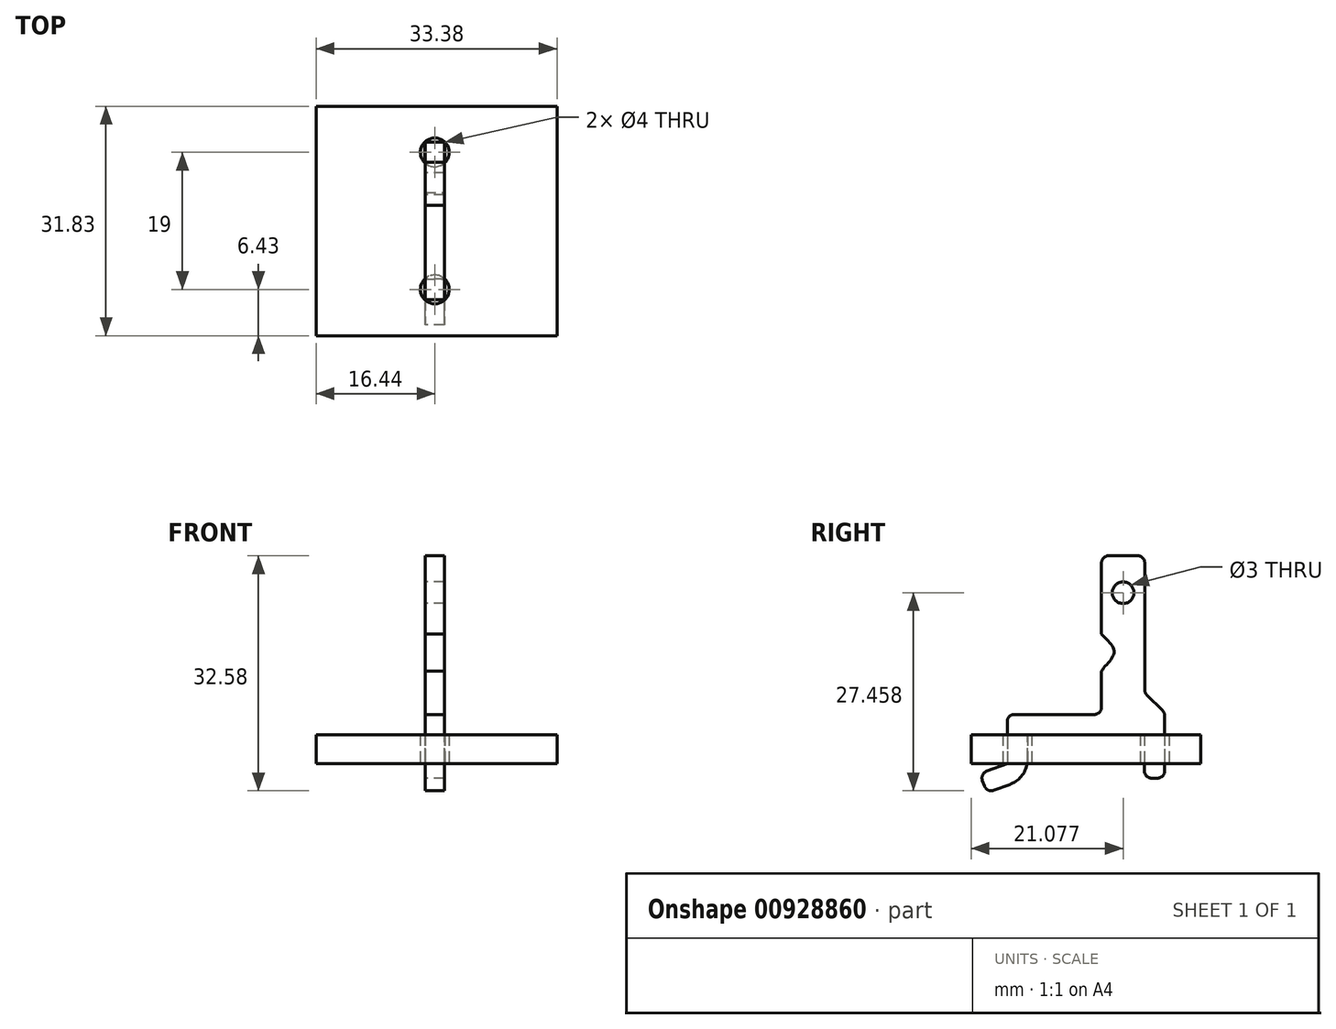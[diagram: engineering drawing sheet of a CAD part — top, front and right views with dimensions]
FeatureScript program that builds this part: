
annotation { "Feature Type Name" : "Feature", "Feature Type Description" : "" }
export const myFeature = defineFeature(function(context is Context, id is Id, definition is map)
    precondition{}
    {
        {
            assignVariable(context, id + "F0", {"name" : "BoardThickness", "anyValue" : 4});
        }
        {
            var Q0;
            Q0=qCreatedBy(makeId("Top.planeOp"),FACE);
            var sketch = newSketch(context, id + "F1", { "sketchPlane" : qUnion([Q0])});
            skCircle(sketch, "E0.cCircle", {"center": v(0, 0) * mm, "radius": 2 * mm});
            skLineSegment(sketch, "E0.0", {"start": v(1.41, 1.41) * mm, "end": v(1.41, -1.41) * mm});
            skLineSegment(sketch, "E0.1", {"start": v(1.41, -1.41) * mm, "end": v(-1.41, -1.41) * mm});
            skLineSegment(sketch, "E0.2", {"start": v(-1.41, -1.41) * mm, "end": v(-1.41, 1.41) * mm});
            skLineSegment(sketch, "E0.3", {"start": v(-1.41, 1.41) * mm, "end": v(1.41, 1.41) * mm});
            skCircle(sketch, "E1.cCircle", {"center": v(0, 19) * mm, "radius": 2 * mm});
            skLineSegment(sketch, "E1.0", {"start": v(1.41, 20.41) * mm, "end": v(1.41, 17.59) * mm});
            skLineSegment(sketch, "E1.1", {"start": v(1.41, 17.59) * mm, "end": v(-1.41, 17.59) * mm});
            skLineSegment(sketch, "E1.2", {"start": v(-1.41, 17.59) * mm, "end": v(-1.41, 20.41) * mm});
            skLineSegment(sketch, "E1.3", {"start": v(-1.41, 20.41) * mm, "end": v(1.41, 20.41) * mm});
            skLineSegment(sketch, "E2.bottom", {"start": v(-16.44, 25.4) * mm, "end": v(16.94, 25.4) * mm});
            skLineSegment(sketch, "E2.top", {"start": v(-16.44, -6.43) * mm, "end": v(16.94, -6.43) * mm});
            skLineSegment(sketch, "E2.left", {"start": v(-16.44, 25.4) * mm, "end": v(-16.44, -6.43) * mm});
            skLineSegment(sketch, "E2.right", {"start": v(16.94, 25.4) * mm, "end": v(16.94, -6.43) * mm});
            skSolve(sketch);
        }
        {
            var Q0;
            Q0=makeQuery(id+"F1.imprint","IMPRINT",FACE,{"disambiguationData":[TD([[makeQuery(id+"F1.imprint","IMPRINT",EDGE,{"derivedFrom":sQuery(id+"F1.wireOp",EDGE,"E2.bottom")}),-1.0]])]});
            extrude(context, id + "F2", {"entities" : qUnion([Q0]), "flatOperationType" : FlatOperationType.REMOVE, "depth" : (getVariable(context, 'BoardThickness')) * mm, "offsetDistance" : 25 * mm, "domain" : OperationDomain.MODEL});
        }
        {
            var Q0;
            Q0=makeQuery(id+"F1.imprint","IMPRINT",FACE,{"disambiguationData":[TD([[makeQuery(id+"F1.imprint","IMPRINT",EDGE,{"derivedFrom":sQuery(id+"F1.wireOp",EDGE,"E0.0")}),-1.0]])]});
            var Q1;
            Q1=makeQuery(id+"F1.imprint","IMPRINT",FACE,{"disambiguationData":[TD([[makeQuery(id+"F1.imprint","IMPRINT",EDGE,{"derivedFrom":sQuery(id+"F1.wireOp",EDGE,"E1.0")}),-1.0]])]});
            extrude(context, id + "F3", {"entities" : qUnion([Q0, Q1]), "flatOperationType" : FlatOperationType.REMOVE, "depth" : 4 * mm, "offsetDistance" : 25 * mm, "domain" : OperationDomain.MODEL});
        }
        {
            var Q0;
            Q0=qCreatedBy(makeId("Right.planeOp"),FACE);
            var sketch = newSketch(context, id + "F4", { "sketchPlane" : qUnion([Q0])});
            skLineSegment(sketch, "E3.0", {"start": v(-1.41, 4) * mm, "end": v(-1.41, 0) * mm});
            skLineSegment(sketch, "E4.0", {"start": v(17.59, 4) * mm, "end": v(17.59, 0) * mm});
            skLineSegment(sketch, "E5.0", {"start": v(1.41, 4) * mm, "end": v(1.41, 0) * mm});
            skLineSegment(sketch, "E6.0", {"start": v(20.41, 4) * mm, "end": v(20.41, 0) * mm});
            skLineSegment(sketch, "E7", {"start": v(1.41, 4) * mm, "end": v(17.59, 4) * mm});
            skLineSegment(sketch, "E8", {"start": v(-1.41, 6.83) * mm, "end": v(11.65, 6.83) * mm});
            skLineSegment(sketch, "E9", {"start": v(11.65, 6.83) * mm, "end": v(11.65, 12.83) * mm});
            skFitSpline(sketch, "E10", {"points": [v(11.65, 12.83) * mm, v(13.41, 15.55) * mm, v(11.65, 17.98) * mm], "startDerivative": vector(3.1, 5.14) * mm, "endDerivative": vector(-3.23, 3.95) * mm});
            skLineSegment(sketch, "E11", {"start": v(11.65, 17.98) * mm, "end": v(11.65, 28.83) * mm});
            skLineSegment(sketch, "E12", {"start": v(11.65, 28.83) * mm, "end": v(17.65, 28.83) * mm});
            skLineSegment(sketch, "E13", {"start": v(17.65, 28.83) * mm, "end": v(17.65, 6.83) * mm});
            skLineSegment(sketch, "E14", {"start": v(17.65, 6.83) * mm, "end": v(20.41, 6.83) * mm});
            skLineSegment(sketch, "E15", {"start": v(20.41, 6.83) * mm, "end": v(20.41, 4) * mm});
            skLineSegment(sketch, "E16", {"start": v(20.41, 0) * mm, "end": v(20.41, -2) * mm});
            skLineSegment(sketch, "E17", {"start": v(20.41, -2) * mm, "end": v(17.59, -2) * mm});
            skLineSegment(sketch, "E18", {"start": v(17.59, -2) * mm, "end": v(17.59, 0) * mm});
            skLineSegment(sketch, "E19", {"start": v(-1.41, 6.83) * mm, "end": v(-1.41, 4) * mm});
            skLineSegment(sketch, "E20", {"start": v(-1.41, 0) * mm, "end": v(-5.2, -1.38) * mm});
            skLineSegment(sketch, "E21", {"start": v(-5.2, -1.38) * mm, "end": v(-4.23, -4.03) * mm});
            skLineSegment(sketch, "E22", {"start": v(-4.23, -4.03) * mm, "end": v(1.41, -1.98) * mm});
            skLineSegment(sketch, "E23", {"start": v(1.41, -1.98) * mm, "end": v(1.41, 0) * mm});
            skCircle(sketch, "E24", {"center": v(14.65, 23.7) * mm, "radius": 1.5 * mm});
            skPoint(sketch, "E24.centerSnap0", {"position": v(14.65, 28.83) * mm});
            skSolve(sketch);
        }
        {
            var Q0;
            Q0=makeQuery(id+"F4.imprint","IMPRINT",FACE,{"disambiguationData":[TD([[makeQuery(id+"F4.imprint","IMPRINT",EDGE,{"derivedFrom":sQuery(id+"F4.wireOp",EDGE,"E3.0")}),1.0]])]});
            extrude(context, id + "F5", {"entities" : qUnion([Q0]), "depth" : 2.7 * mm, "offsetDistance" : 25 * mm, "symmetric" : true});
        }
        {
            var Q0;
            Q0=makeQuery(id+"F5.opExtrude","SWEPT_EDGE",EDGE,{"disambiguationData":[OSD([sQuery(id+"F4.wireOp",EDGE,"E13"),sQuery(id+"F4.wireOp",EDGE,"E14")])]});
            chamfer(context, id + "F6", {"entities" : qUnion([Q0]), "width" : 3 * mm, "tangentPropagation" : true});
        }
        {
            var Q0;
            Q0=makeQuery(id+"F5.opExtrude","SWEPT_EDGE",EDGE,{"disambiguationData":[OSD([sQuery(id+"F4.wireOp",EDGE,"E22"),sQuery(id+"F4.wireOp",EDGE,"E23")])]});
            fillet(context, id + "F7", {"entities" : qUnion([Q0]), "radius" : 3.8 * mm, "tangentPropagation" : true, "allowEdgeOverflow" : false});
        }
        {
            var Q0;
            Q0=makeQuery(id+"F5.opExtrude","SWEPT_EDGE",EDGE,{"disambiguationData":[OSD([sQuery(id+"F4.wireOp",EDGE,"E20"),sQuery(id+"F4.wireOp",EDGE,"E21")])]});
            var Q1;
            Q1=makeQuery(id+"F5.opExtrude","SWEPT_EDGE",EDGE,{"disambiguationData":[OSD([sQuery(id+"F4.wireOp",EDGE,"E21"),sQuery(id+"F4.wireOp",EDGE,"E22")])]});
            var Q2;
            Q2=makeQuery(id+"F5.opExtrude","SWEPT_EDGE",EDGE,{"disambiguationData":[OSD([sQuery(id+"F4.wireOp",EDGE,"E8"),sQuery(id+"F4.wireOp",EDGE,"E19")])]});
            var Q3;
            Q3=makeQuery(id+"F5.opExtrude","SWEPT_EDGE",EDGE,{"disambiguationData":[OSD([sQuery(id+"F4.wireOp",EDGE,"E8"),sQuery(id+"F4.wireOp",EDGE,"E9")])]});
            var Q4;
            Q4=makeQuery(id+"F5.opExtrude","SWEPT_EDGE",EDGE,{"disambiguationData":[OSD([sQuery(id+"F4.wireOp",EDGE,"E11"),sQuery(id+"F4.wireOp",EDGE,"E12")])]});
            var Q5;
            Q5=makeQuery(id+"F5.opExtrude","SWEPT_EDGE",EDGE,{"disambiguationData":[OSD([sQuery(id+"F4.wireOp",EDGE,"E12"),sQuery(id+"F4.wireOp",EDGE,"E13")])]});
            var Q6;
            Q6=makeQuery(id+"F5.opExtrude","SWEPT_EDGE",EDGE,{"disambiguationData":[OSD([sQuery(id+"F4.wireOp",EDGE,"E17"),sQuery(id+"F4.wireOp",EDGE,"E18")])]});
            var Q7;
            Q7=makeQuery(id+"F5.opExtrude","SWEPT_EDGE",EDGE,{"disambiguationData":[OSD([sQuery(id+"F4.wireOp",EDGE,"E16"),sQuery(id+"F4.wireOp",EDGE,"E17")])]});
            var Q8;
            Q8=makeQuery(id+"F6.opChamfer","BLEND_EDGE",EDGE,{"blendedFrom":[makeQuery(id+"F5.opExtrude","SWEPT_EDGE",EDGE,{"disambiguationData":[OSD([sQuery(id+"F4.wireOp",EDGE,"E13"),sQuery(id+"F4.wireOp",EDGE,"E14")])]}),makeQuery(id+"F5.opExtrude","SWEPT_FACE",FACE,{"disambiguationData":[OSD([sQuery(id+"F4.wireOp",EDGE,"E6.0"),sQuery(id+"F4.wireOp",EDGE,"E15"),sQuery(id+"F4.wireOp",EDGE,"E16")])]})],"blendedInto":[makeQuery(id+"F5.opExtrude","SWEPT_FACE",FACE,{"disambiguationData":[OSD([sQuery(id+"F4.wireOp",EDGE,"E6.0"),sQuery(id+"F4.wireOp",EDGE,"E15"),sQuery(id+"F4.wireOp",EDGE,"E16")])]})]});
            var Q9;
            {var subQ0=sQuery(id+"F4.wireOp",EDGE,"E13");Q9=makeQuery(id+"F6.opChamfer","BLEND_EDGE",EDGE,{"blendedFrom":[makeQuery(id+"F5.opExtrude","SWEPT_EDGE",EDGE,{"disambiguationData":[OSD([subQ0,sQuery(id+"F4.wireOp",EDGE,"E14")])]}),makeQuery(id+"F5.opExtrude","SWEPT_FACE",FACE,{"disambiguationData":[OSD([subQ0])]})],"blendedInto":[makeQuery(id+"F5.opExtrude","SWEPT_FACE",FACE,{"disambiguationData":[OSD([subQ0])]})]});}
            fillet(context, id + "F8", {"entities" : qUnion([Q0, Q1, Q2, Q3, Q4, Q5, Q6, Q7, Q8, Q9]), "radius" : 1 * mm, "tangentPropagation" : true, "allowEdgeOverflow" : false});
        }
    });
